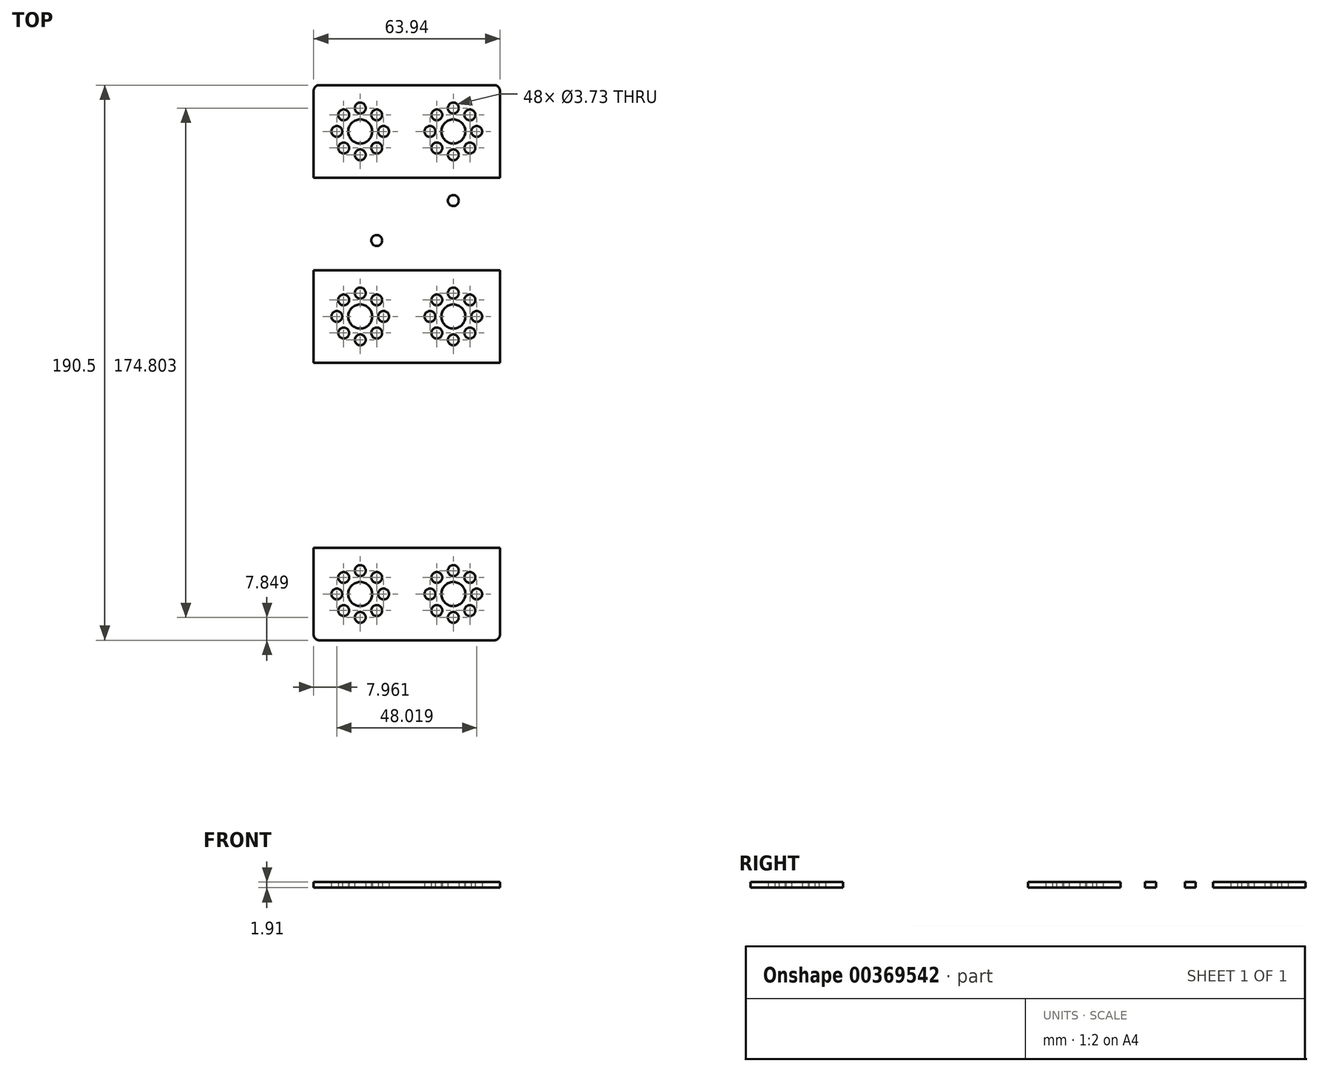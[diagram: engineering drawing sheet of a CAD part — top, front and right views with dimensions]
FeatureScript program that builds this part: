
annotation { "Feature Type Name" : "Feature", "Feature Type Description" : "" }
export const myFeature = defineFeature(function(context is Context, id is Id, definition is map)
    precondition{}
    {
        {
            var Q0;
            Q0=qCreatedBy(makeId("Top.planeOp"),FACE);
            var sketch = newSketch(context, id + "F0", { "sketchPlane" : qUnion([Q0])});
            skLineSegment(sketch, "E0.bottom", {"start": v(30.06, -95.25) * mm, "end": v(-30.06, -95.25) * mm});
            skLineSegment(sketch, "E0.top", {"start": v(30.06, 95.25) * mm, "end": v(-30.06, 95.25) * mm});
            skLineSegment(sketch, "E0.left", {"start": v(31.97, -93.35) * mm, "end": v(31.97, 93.35) * mm});
            skLineSegment(sketch, "E0.right", {"start": v(-31.97, -93.35) * mm, "end": v(-31.97, 93.34) * mm});
            skPoint(sketch, "E0.middle", {"position": v(0, 0) * mm});
            skPoint(sketch, "E1.visualSharp", {"position": v(-31.97, 95.25) * mm});
            skArc(sketch, "E1.filletArc", {"start": v(-30.06, 95.25) * mm, "mid": v(-31.4, 94.7) * mm, "end": v(-31.97, 93.34) * mm});
            skPoint(sketch, "E2.visualSharp", {"position": v(-31.97, -95.25) * mm});
            skArc(sketch, "E2.filletArc", {"start": v(-31.97, -93.35) * mm, "mid": v(-31.4, -94.7) * mm, "end": v(-30.06, -95.25) * mm});
            skPoint(sketch, "E3.visualSharp", {"position": v(31.97, 95.25) * mm});
            skArc(sketch, "E3.filletArc", {"start": v(31.97, 93.35) * mm, "mid": v(31.4, 94.7) * mm, "end": v(30.06, 95.25) * mm});
            skPoint(sketch, "E4.visualSharp", {"position": v(31.97, -95.25) * mm});
            skArc(sketch, "E4.filletArc", {"start": v(30.06, -95.25) * mm, "mid": v(31.4, -94.7) * mm, "end": v(31.97, -93.35) * mm});
            skLineSegment(sketch, "E5", {"start": v(0, 95.25) * mm, "end": v(0, 0) * mm});
            skLineSegment(sketch, "E6", {"start": v(-31.97, 0) * mm, "end": v(31.97, 0) * mm});
            skPoint(sketch, "E7", {"position": v(0, 63.5) * mm});
            skPoint(sketch, "E8", {"position": v(0, 31.75) * mm});
            skPoint(sketch, "E9", {"position": v(0, -31.75) * mm});
            skPoint(sketch, "E10", {"position": v(0, -63.5) * mm});
            skPoint(sketch, "E11", {"position": v(-31.97, 63.5) * mm});
            skPoint(sketch, "E12", {"position": v(-31.97, 31.75) * mm});
            skPoint(sketch, "E13", {"position": v(-31.97, -31.75) * mm});
            skPoint(sketch, "E14", {"position": v(-31.97, -63.5) * mm});
            skLineSegment(sketch, "E15", {"start": v(-31.97, 63.5) * mm, "end": v(31.97, 63.5) * mm});
            skLineSegment(sketch, "E16", {"start": v(-31.97, 31.75) * mm, "end": v(31.97, 31.75) * mm});
            skLineSegment(sketch, "E17", {"start": v(-31.97, -63.5) * mm, "end": v(31.97, -63.5) * mm});
            skCircle(sketch, "E18", {"center": v(15.98, 79.38) * mm, "radius": 4.13 * mm});
            skCircle(sketch, "E19", {"center": v(15.98, 71.35) * mm, "radius": 1.87 * mm});
            skCircle(sketch, "E20", {"center": v(21.66, 73.7) * mm, "radius": 1.87 * mm});
            skCircle(sketch, "E21", {"center": v(24, 79.37) * mm, "radius": 1.87 * mm});
            skCircle(sketch, "E22", {"center": v(15.98, 87.4) * mm, "radius": 1.87 * mm});
            skLineSegment(sketch, "E23", {"start": v(0, 95.25) * mm, "end": v(31.97, 95.25) * mm});
            skCircle(sketch, "E24", {"center": v(21.66, 85.05) * mm, "radius": 1.87 * mm});
            skCircle(sketch, "E25.MirrorC", {"center": v(10.3, 73.7) * mm, "radius": 1.87 * mm});
            skCircle(sketch, "E26.MirrorC", {"center": v(7.96, 79.37) * mm, "radius": 1.87 * mm});
            skCircle(sketch, "E27.MirrorC", {"center": v(10.3, 85.05) * mm, "radius": 1.87 * mm});
            skPoint(sketch, "E28.orphan", {"position": v(15.98, 63.5) * mm});
            skPoint(sketch, "E29.start.orphan", {"position": v(15.98, 95.25) * mm});
            skCircle(sketch, "E30.MirrorC", {"center": v(15.98, 55.65) * mm, "radius": 1.87 * mm});
            skCircle(sketch, "E31.MirrorC", {"center": v(10.3, 53.3) * mm, "radius": 1.87 * mm});
            skCircle(sketch, "E32.MirrorC", {"center": v(21.66, 53.3) * mm, "radius": 1.87 * mm});
            skCircle(sketch, "E33.MirrorC", {"center": v(24, 47.62) * mm, "radius": 1.87 * mm});
            skCircle(sketch, "E34.MirrorC", {"center": v(15.98, 39.6) * mm, "radius": 1.87 * mm});
            skCircle(sketch, "E35.MirrorC", {"center": v(10.3, 41.95) * mm, "radius": 1.87 * mm});
            skCircle(sketch, "E36.MirrorC", {"center": v(7.96, 47.62) * mm, "radius": 1.87 * mm});
            skCircle(sketch, "E37.MirrorC", {"center": v(21.66, 41.95) * mm, "radius": 1.87 * mm});
            skCircle(sketch, "E38.MirrorC", {"center": v(15.98, 47.62) * mm, "radius": 4.13 * mm});
            skCircle(sketch, "E39.MirrorC", {"center": v(-15.98, 47.62) * mm, "radius": 4.13 * mm});
            skCircle(sketch, "E40.MirrorC", {"center": v(-10.3, 41.95) * mm, "radius": 1.87 * mm});
            skCircle(sketch, "E41.MirrorC", {"center": v(-7.96, 47.62) * mm, "radius": 1.87 * mm});
            skCircle(sketch, "E42.MirrorC", {"center": v(-15.98, 39.6) * mm, "radius": 1.87 * mm});
            skCircle(sketch, "E43.MirrorC", {"center": v(-21.66, 41.95) * mm, "radius": 1.87 * mm});
            skCircle(sketch, "E44.MirrorC", {"center": v(-24, 47.62) * mm, "radius": 1.87 * mm});
            skCircle(sketch, "E45.MirrorC", {"center": v(-21.66, 53.3) * mm, "radius": 1.87 * mm});
            skCircle(sketch, "E46.MirrorC", {"center": v(-15.98, 55.65) * mm, "radius": 1.87 * mm});
            skCircle(sketch, "E47.MirrorC", {"center": v(-10.3, 53.3) * mm, "radius": 1.87 * mm});
            skCircle(sketch, "E48.MirrorC", {"center": v(-10.3, 73.7) * mm, "radius": 1.87 * mm});
            skCircle(sketch, "E49.MirrorC", {"center": v(-7.96, 79.37) * mm, "radius": 1.87 * mm});
            skCircle(sketch, "E50.MirrorC", {"center": v(-10.3, 85.05) * mm, "radius": 1.87 * mm});
            skCircle(sketch, "E51.MirrorC", {"center": v(-15.98, 87.4) * mm, "radius": 1.87 * mm});
            skCircle(sketch, "E52.MirrorC", {"center": v(-21.66, 85.05) * mm, "radius": 1.87 * mm});
            skCircle(sketch, "E53.MirrorC", {"center": v(-21.66, 73.7) * mm, "radius": 1.87 * mm});
            skCircle(sketch, "E54.MirrorC", {"center": v(-24, 79.37) * mm, "radius": 1.87 * mm});
            skCircle(sketch, "E55.MirrorC", {"center": v(-15.98, 71.35) * mm, "radius": 1.87 * mm});
            skCircle(sketch, "E56.MirrorC", {"center": v(-15.98, 79.38) * mm, "radius": 4.13 * mm});
            skCircle(sketch, "E57.MirrorC", {"center": v(15.98, -39.6) * mm, "radius": 1.87 * mm});
            skPoint(sketch, "E58.trimOffspring.end.orphan", {"position": v(0, -95.25) * mm});
            skCircle(sketch, "E59.MirrorC", {"center": v(15.98, 23.9) * mm, "radius": 1.87 * mm});
            skCircle(sketch, "E60.MirrorC", {"center": v(21.66, 21.55) * mm, "radius": 1.87 * mm});
            skCircle(sketch, "E61.MirrorC", {"center": v(24, 15.88) * mm, "radius": 1.87 * mm});
            skCircle(sketch, "E62.MirrorC", {"center": v(21.66, 10.2) * mm, "radius": 1.87 * mm});
            skCircle(sketch, "E63.MirrorC", {"center": v(15.98, 7.85) * mm, "radius": 1.87 * mm});
            skCircle(sketch, "E64.MirrorC", {"center": v(10.3, 10.2) * mm, "radius": 1.87 * mm});
            skCircle(sketch, "E65.MirrorC", {"center": v(7.96, 15.88) * mm, "radius": 1.87 * mm});
            skCircle(sketch, "E66.MirrorC", {"center": v(10.3, 21.55) * mm, "radius": 1.87 * mm});
            skCircle(sketch, "E67.MirrorC", {"center": v(15.98, 15.88) * mm, "radius": 4.13 * mm});
            skCircle(sketch, "E68.MirrorC", {"center": v(-10.3, 21.55) * mm, "radius": 1.87 * mm});
            skCircle(sketch, "E69.MirrorC", {"center": v(-15.98, 23.9) * mm, "radius": 1.87 * mm});
            skCircle(sketch, "E70.MirrorC", {"center": v(-7.96, 15.88) * mm, "radius": 1.87 * mm});
            skCircle(sketch, "E71.MirrorC", {"center": v(-10.3, 10.2) * mm, "radius": 1.87 * mm});
            skCircle(sketch, "E72.MirrorC", {"center": v(-15.98, 7.85) * mm, "radius": 1.87 * mm});
            skCircle(sketch, "E73.MirrorC", {"center": v(-24, 15.87) * mm, "radius": 1.87 * mm});
            skCircle(sketch, "E74.MirrorC", {"center": v(-21.66, 21.55) * mm, "radius": 1.87 * mm});
            skCircle(sketch, "E75.MirrorC", {"center": v(-15.98, 15.88) * mm, "radius": 4.13 * mm});
            skCircle(sketch, "E76.MirrorC", {"center": v(-21.66, 10.2) * mm, "radius": 1.87 * mm});
            skSolve(sketch);
        }
        {
            var Q0;
            Q0=makeQuery(id+"F0.imprint","IMPRINT",FACE,{"disambiguationData":[TD([[makeQuery(id+"F0.imprint","IMPRINT",EDGE,{"derivedFrom":sQuery(id+"F0.wireOp",EDGE,"E40.MirrorC")}),1.0]])]});
            var Q1;
            {var subQ1=sQuery(id+"F0.wireOp",EDGE,"E0.top");Q1=makeQuery(id+"F0.imprint","IMPRINT",FACE,{"disambiguationData":[TD([[makeQuery(id+"F0.imprint","IMPRINT",EDGE,{"derivedFrom":subQ1}),1.0]])]});}
            var Q2;
            {var subQ3=sQuery(id+"F0.wireOp",EDGE,"E3.filletArc");Q2=makeQuery(id+"F0.imprint","IMPRINT",FACE,{"disambiguationData":[TD([[makeQuery(id+"F0.imprint","IMPRINT",EDGE,{"derivedFrom":subQ3}),1.0]])]});}
            var Q3;
            Q3=makeQuery(id+"F0.imprint","IMPRINT",FACE,{"disambiguationData":[TD([[makeQuery(id+"F0.imprint","IMPRINT",EDGE,{"derivedFrom":sQuery(id+"F0.wireOp",EDGE,"E30.MirrorC")}),1.0]])]});
            var Q4;
            {var subQ0=sQuery(id+"F0.wireOp",EDGE,"E6");var subQ1=sQuery(id+"F0.wireOp",EDGE,"E0.left");var subQ2=makeQuery(id+"F0.imprint","INTERSECT",VERTEX,{"derivedFrom":[subQ1,subQ0]});Q4=makeQuery(id+"F0.imprint","IMPRINT",FACE,{"disambiguationData":[TD([[makeQuery(id+"F0.imprint","IMPRINT",EDGE,{"disambiguationData":[TD([[subQ2,-1.0]])],"derivedFrom":subQ1}),1.0]])]});}
            var Q5;
            {var subQ0=sQuery(id+"F0.wireOp",EDGE,"E6");var subQ1=sQuery(id+"F0.wireOp",EDGE,"E0.right");var subQ2=makeQuery(id+"F0.imprint","INTERSECT",VERTEX,{"derivedFrom":[subQ1,subQ0]});Q5=makeQuery(id+"F0.imprint","IMPRINT",FACE,{"disambiguationData":[TD([[makeQuery(id+"F0.imprint","IMPRINT",EDGE,{"disambiguationData":[TD([[subQ2,-1.0]])],"derivedFrom":subQ1}),-1.0]])]});}
            extrude(context, id + "F1", {"entities" : qUnion([Q0, Q1, Q2, Q3, Q4, Q5]), "depth" : 1.9 * mm});
        }
        {
            var Q0;
            Q0=makeQuery(id+"F1.opExtrude","SWEPT_BODY",BODY,{"disambiguationData":[OSD([sQuery(id+"F0.wireOp",EDGE,"E0.top"),sQuery(id+"F0.wireOp",EDGE,"E0.left"),sQuery(id+"F0.wireOp",EDGE,"E0.right"),sQuery(id+"F0.wireOp",EDGE,"E1.filletArc"),sQuery(id+"F0.wireOp",EDGE,"E3.filletArc"),sQuery(id+"F0.wireOp",EDGE,"E6"),sQuery(id+"F0.wireOp",EDGE,"E18"),sQuery(id+"F0.wireOp",EDGE,"E19"),sQuery(id+"F0.wireOp",EDGE,"E20"),sQuery(id+"F0.wireOp",EDGE,"E21"),sQuery(id+"F0.wireOp",EDGE,"E22"),sQuery(id+"F0.wireOp",EDGE,"E23"),sQuery(id+"F0.wireOp",EDGE,"E24"),sQuery(id+"F0.wireOp",EDGE,"E25.MirrorC"),sQuery(id+"F0.wireOp",EDGE,"E26.MirrorC"),sQuery(id+"F0.wireOp",EDGE,"E27.MirrorC"),sQuery(id+"F0.wireOp",EDGE,"E30.MirrorC"),sQuery(id+"F0.wireOp",EDGE,"E31.MirrorC"),sQuery(id+"F0.wireOp",EDGE,"E32.MirrorC"),sQuery(id+"F0.wireOp",EDGE,"E33.MirrorC"),sQuery(id+"F0.wireOp",EDGE,"E34.MirrorC"),sQuery(id+"F0.wireOp",EDGE,"E35.MirrorC"),sQuery(id+"F0.wireOp",EDGE,"E36.MirrorC"),sQuery(id+"F0.wireOp",EDGE,"E37.MirrorC"),sQuery(id+"F0.wireOp",EDGE,"E38.MirrorC"),sQuery(id+"F0.wireOp",EDGE,"E40.MirrorC"),sQuery(id+"F0.wireOp",EDGE,"E39.MirrorC"),sQuery(id+"F0.wireOp",EDGE,"E41.MirrorC"),sQuery(id+"F0.wireOp",EDGE,"E42.MirrorC"),sQuery(id+"F0.wireOp",EDGE,"E43.MirrorC"),sQuery(id+"F0.wireOp",EDGE,"E44.MirrorC"),sQuery(id+"F0.wireOp",EDGE,"E45.MirrorC"),sQuery(id+"F0.wireOp",EDGE,"E46.MirrorC"),sQuery(id+"F0.wireOp",EDGE,"E47.MirrorC"),sQuery(id+"F0.wireOp",EDGE,"E48.MirrorC"),sQuery(id+"F0.wireOp",EDGE,"E49.MirrorC"),sQuery(id+"F0.wireOp",EDGE,"E50.MirrorC"),sQuery(id+"F0.wireOp",EDGE,"E52.MirrorC"),sQuery(id+"F0.wireOp",EDGE,"E51.MirrorC"),sQuery(id+"F0.wireOp",EDGE,"E53.MirrorC"),sQuery(id+"F0.wireOp",EDGE,"E54.MirrorC"),sQuery(id+"F0.wireOp",EDGE,"E55.MirrorC"),sQuery(id+"F0.wireOp",EDGE,"E56.MirrorC"),sQuery(id+"F0.wireOp",EDGE,"E61.MirrorC"),sQuery(id+"F0.wireOp",EDGE,"E60.MirrorC"),sQuery(id+"F0.wireOp",EDGE,"E62.MirrorC"),sQuery(id+"F0.wireOp",EDGE,"E63.MirrorC"),sQuery(id+"F0.wireOp",EDGE,"E64.MirrorC"),sQuery(id+"F0.wireOp",EDGE,"E65.MirrorC"),sQuery(id+"F0.wireOp",EDGE,"E59.MirrorC"),sQuery(id+"F0.wireOp",EDGE,"E66.MirrorC"),sQuery(id+"F0.wireOp",EDGE,"E67.MirrorC"),sQuery(id+"F0.wireOp",EDGE,"E68.MirrorC"),sQuery(id+"F0.wireOp",EDGE,"E70.MirrorC"),sQuery(id+"F0.wireOp",EDGE,"E69.MirrorC"),sQuery(id+"F0.wireOp",EDGE,"E72.MirrorC"),sQuery(id+"F0.wireOp",EDGE,"E71.MirrorC"),sQuery(id+"F0.wireOp",EDGE,"E74.MirrorC"),sQuery(id+"F0.wireOp",EDGE,"E73.MirrorC"),sQuery(id+"F0.wireOp",EDGE,"E75.MirrorC"),sQuery(id+"F0.wireOp",EDGE,"E76.MirrorC")])]});
            var Q1;
            Q1=qCreatedBy(makeId("Front.planeOp"),FACE);
            mirror(context, id + "F2", {"operationType" : NewBodyOperationType.ADD, "entities" : qUnion([Q0]), "mirrorPlane" : qUnion([Q1])});
        }
    });
